# Revit family: Hager-Orion_Plus-IP65-D300-Cl.II-Poly_double_encl-630A-Floor_installation-NoHosted-PL-pl
name_source: partatom
category: Electrical Equipment
units: mm (PartAtom-declared; Revit-internal decimal feet)

## family parameters
Always vertical = Yes
Cut with Voids When Loaded = No
Panel Configuration = Two Columns, Circuits Across
Part Type = Panelboard
Room Calculation Point = No
Round Connector Dimension = Use Diameter
Shared = No
Work Plane-Based = Yes

## types (15) — shared parameters
Default Elevation = 1219 mm
EF000003 - Sposób montażu = EV012274 - Montaż podłogowy
EF000007 - Kolor = EV000270 - Szary
EF000049 - Głębokość = 300 mm  [stored 0.984252 ft]
EF000116 - Numer RAL = 7035
EF001131 - Głębokość wewnętrzna = 300 mm  [stored 0.984252 ft]
EF001596 - Materiał obudowy = EV000139 - Tworzywo sztuczne
EF001613 - Podtrzymanie funkcji = EV000494 - Brak
EF005474 - Stopień ochrony (IP) = EV006421 - IP65
EF006306 - Z zamkiem = Yes
EF007800 - Do ochrony odgromowej = No
EF008873 - Prąd znamionowy (In) = 630 A
EF009170 - Obudowa z materiału o wysokiej wytrzymałości mechanicznej = 2 mm  [stored 0.00656168 ft]
EF009171 - Drzwi/pokrywa z materiału o wysokiej wytrzymałości mechanicznej = 2 mm  [stored 0.00656168 ft]
EF015940 - Pokrywa z wyzwalaczem nadciśnieniowym = No
HG000003 - Zakres = Orion Plus
HG000006 - Montaż podtynkowy = No
HG000010 - Drzwi asymetryczne = No
HG000023 - Obudowa dwusekcyjna = Yes
HG000024 - Wysokość części dolnej = 600 mm
HG000026 - Stojąca = No
HG000027 - Wysokość cokołu = 70 mm  [stored 0.229659 ft]
Manufacturer = Hager
Type Comments = Orion Plus
zero-valued in all types: EF000218 - Głębokość wbudowania, EF000437 - Liczba wejść kablowych, EF009554 - Liczba otworów pod flansze

## per-type parameters (varying)
| type | EF000008 - Szerokość | EF000040 - Wysokość | EF000118 - Z płytą montażową | EF000266 - Liczba rzędów | EF000339 - Rodzaj pokrywy | EF001088 - Możliwość rozbudowy | EF002950 - Szerokość wyrażona liczbą modułów | EF003532 - Do zastosowań zewnętrznych | EF004293 - Odporność udarowa | EF004427 - Liczba modułów | EF004464 - Rodzaj drzwi | EF006244 - Transparentna pokrywa/drzwi | EF009212 - Wykonanie pokrywy | HG000002 - Z drzwiami lub pokrywą | HG000004 - Referencja producenta | HG000009 - Drzwi dwuskrzydłowe |
| Montaż podłogowy IP65 S1100 W1150 G300  - FL360B | 1100 mm | 1150 mm | No | 3 | EV004216 - Drzwi | Yes | 0 | Yes | EV008784 - IK10 | 138 | EV002646 - Pojedynczy | Yes | EV009916 - Z otworem | Yes | FL360B | Yes |
| Montaż podłogowy IP65 S1100 W1450 G300  - FL362B | 1100 mm | 1450 mm  [stored 4.75722 ft] | No | 3 | EV004216 - Drzwi | Yes | 0 | Yes | EV008784 - IK10 | 138 | EV002646 - Pojedynczy | Yes | EV009916 - Z otworem | Yes | FL362B | Yes |
| Montaż podłogowy IP65 S1100 W1750 G300  - FL364B | 1100 mm | 1750 mm  [stored 5.74147 ft] | No | 3 | EV004216 - Drzwi | Yes | 0 | Yes | EV008784 - IK10 | 138 | EV002646 - Pojedynczy | Yes | EV009916 - Z otworem | Yes | FL364B | Yes |
| Montaż podłogowy IP65 S1100 W1750 G300  - FL366B | 1100 mm | 1750 mm  [stored 5.74147 ft] | No | 5 | EV004216 - Drzwi | Yes | 0 | Yes | EV008784 - IK10 | 230 | EV002646 - Pojedynczy | Yes | EV009916 - Z otworem | Yes | FL366B | Yes |
| Montaż podłogowy IP65 S1100 W2050 G300  - FL368B | 1100 mm | 2050 mm  [stored 6.72572 ft] | Yes | 5 | EV001012 - Pokrywa | No | 0 | No | EV006814 - IK08 | 230 | EV002646 - Pojedynczy | No | EV000116 - Zamknięty | Yes | FL368B | Yes |
| Montaż podłogowy IP65 S600 W1150 G300  - FL340B | 600 mm | 1150 mm | No | 3 | EV004216 - Drzwi | Yes | 0 | Yes | EV008784 - IK10 | 69 | EV002646 - Pojedynczy | Yes | EV009916 - Z otworem | Yes | FL340B | No |
| Montaż podłogowy IP65 S600 W1450 G300  - FL342B | 600 mm | 1450 mm  [stored 4.75722 ft] | No | 3 | EV004216 - Drzwi | Yes | 0 | Yes | EV008784 - IK10 | 69 | EV002646 - Pojedynczy | Yes | EV009916 - Z otworem | No | FL342B | No |
| Montaż podłogowy IP65 S600 W1750 G300  - FL344B | 600 mm | 1750 mm  [stored 5.74147 ft] | No | 9 | EV004216 - Drzwi | Yes | 23 | No |  | 0 |  | Yes | EV009916 - Z otworem | Yes | FL344B | No |
| Montaż podłogowy IP65 S600 W1750 G300  - FL346B | 600 mm | 1750 mm  [stored 5.74147 ft] | No | 5 | EV004216 - Drzwi | Yes | 0 | Yes | EV008784 - IK10 | 115 | EV002646 - Pojedynczy | Yes | EV009916 - Z otworem | Yes | FL346B | No |
| Montaż podłogowy IP65 S600 W2050 G300  - FL348B | 600 mm | 2050 mm  [stored 6.72572 ft] | No | 3 | EV004216 - Drzwi | Yes | 0 | Yes | EV008784 - IK10 | 115 | EV002646 - Pojedynczy | Yes | EV009916 - Z otworem | Yes | FL348B | No |
| Montaż podłogowy IP65 S850 W1150 G300  - FL350B | 850 mm  [stored 2.78871 ft] | 1150 mm | No | 3 | EV004216 - Drzwi | Yes | 0 | Yes | EV008784 - IK10 | 111 | EV002646 - Pojedynczy | Yes | EV009916 - Z otworem | Yes | FL350B | No |
| Montaż podłogowy IP65 S850 W1450 G300  - FL352B | 850 mm  [stored 2.78871 ft] | 1450 mm  [stored 4.75722 ft] | Yes | 3 | EV001012 - Pokrywa | No | 0 | No | EV006814 - IK08 | 111 | EV002646 - Pojedynczy | No | EV000116 - Zamknięty | Yes | FL352B | No |
| Montaż podłogowy IP65 S850 W1750 G300  - FL354B | 850 mm  [stored 2.78871 ft] | 1750 mm  [stored 5.74147 ft] | Yes | 3 | EV001012 - Pokrywa | No | 0 | No | EV006814 - IK08 | 111 | EV002646 - Pojedynczy | No | EV000116 - Zamknięty | Yes | FL354B | No |
| Montaż podłogowy IP65 S850 W1750 G300  - FL356B | 850 mm  [stored 2.78871 ft] | 1750 mm  [stored 5.74147 ft] | No | 5 | EV004216 - Drzwi | Yes | 0 | Yes | EV008784 - IK10 | 185 | EV002646 - Pojedynczy | Yes | EV009916 - Z otworem | Yes | FL356B | No |
| Montaż podłogowy IP65 S850 W2050 G300  - FL358B | 850 mm  [stored 2.78871 ft] | 2050 mm  [stored 6.72572 ft] | No | 5 | EV004216 - Drzwi | Yes | 0 | Yes | EV008784 - IK10 | 185 | EV002646 - Pojedynczy | Yes | EV009916 - Z otworem | Yes | FL358B | No |

note: [stored X ft] marks values corroborated as IEEE doubles in the binary element streams (Revit-internal decimal feet)

## geometry (parser evidence)
native form markers: Blend x4, Sweep x5
no freeform markers — native parametric forms only
